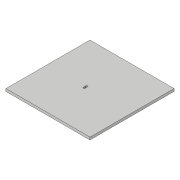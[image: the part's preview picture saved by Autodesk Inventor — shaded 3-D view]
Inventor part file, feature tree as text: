
AUTODESK INVENTOR PART (.ipt)
format: ipt  version: 2017 (Build 210142000, 142)  size: 90,624 bytes
history: native  units: in
note: dims shown in document units (in); Inventor stores cm internally (conversion verified against a paired STEP export)
features: sketch x2, other x2, sheet_metal_op x1
ambient origin geometry x8: Origin, YZ Plane, XZ Plane, XY Plane, X Axis, Y Axis, Z Axis, Center Point
bodies: Solid1 (feature_tree)
feature tree (5):
  sheet_metal_op  "Face1"
  sketch  "Sketch1"  dims[d0=4.0in]
  other  "Plate1"
  sketch  "Sketch2"  dims[d1=4.0in d2=0.12in d3=0.04in d4=0.12in d5=0.12in d6=0.0in]
  other  "Cut1"
